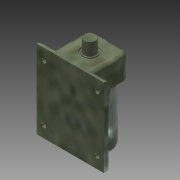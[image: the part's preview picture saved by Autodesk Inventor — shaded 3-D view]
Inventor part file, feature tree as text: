
AUTODESK INVENTOR PART (.ipt)
format: ipt  version: 2015 (Build 190159000, 159)  size: 245,248 bytes
history: native  units: mm
features: extrude x6, sketch x6, fillet x5, plane x1
ambient origin geometry x8: Origin, YZ Plane, XZ Plane, XY Plane, X Axis, Y Axis, Z Axis, Center Point
bodies: 实体1 (feature_tree)
feature tree (18):
  extrude  "拉伸1"  Depth=8.0mm
  extrude  "拉伸2"  Depth=10.0mm TaperAngle=0.0deg
  fillet  "圆角1"  Radius=70.0mm
  fillet  "圆角2"  Radius=100.0mm
  fillet  "圆角3"  Radius=10.0mm
  fillet  "圆角4"  Radius=5.5mm
  extrude  "拉伸3"  Depth=5.0mm
  extrude  "拉伸4"  Depth=22.0mm TaperAngle=0.0deg
  fillet  "圆角5"  Radius=21.0mm
  extrude  "拉伸5"  Depth=25.0mm
  plane  "工作平面1"
  extrude  "拉伸6"  Depth=2.0mm TaperAngle=0.0deg
  sketch  "草图1"  dims[d0=70.0mm d1=8.0mm]
  sketch  "草图2"  dims[d2=120.0mm d3=140.0mm d4=0.0mm d5=70.0mm d6=100.0mm d7=0.0mm d8=10.0mm d9=5.5mm]
  sketch  "草图3"  dims[d10=5.0mm d11=5.0mm]
  sketch  "草图4"  dims[d12=20.0mm d13=22.0mm d14=0.0mm d15=21.0mm]
  sketch  "草图5"  dims[d16=20.0mm d17=25.0mm]
  sketch  "草图6"  dims[d18=30.0mm d19=2.0mm d20=0.0mm d21=0.5mm d22=8.0mm d23=8.0mm d24=8.0mm d25=8.0mm d26=12.5mm d27=12.5mm d28=12.5mm d29=12.5mm d30=20.0mm d31=20.0mm d32=20.0mm d33=20.0mm d34=2.0mm d35=0.0mm d36=4.0mm d37=10.0mm d38=10.212526mm d39=2.0mm d40=0.0mm]
